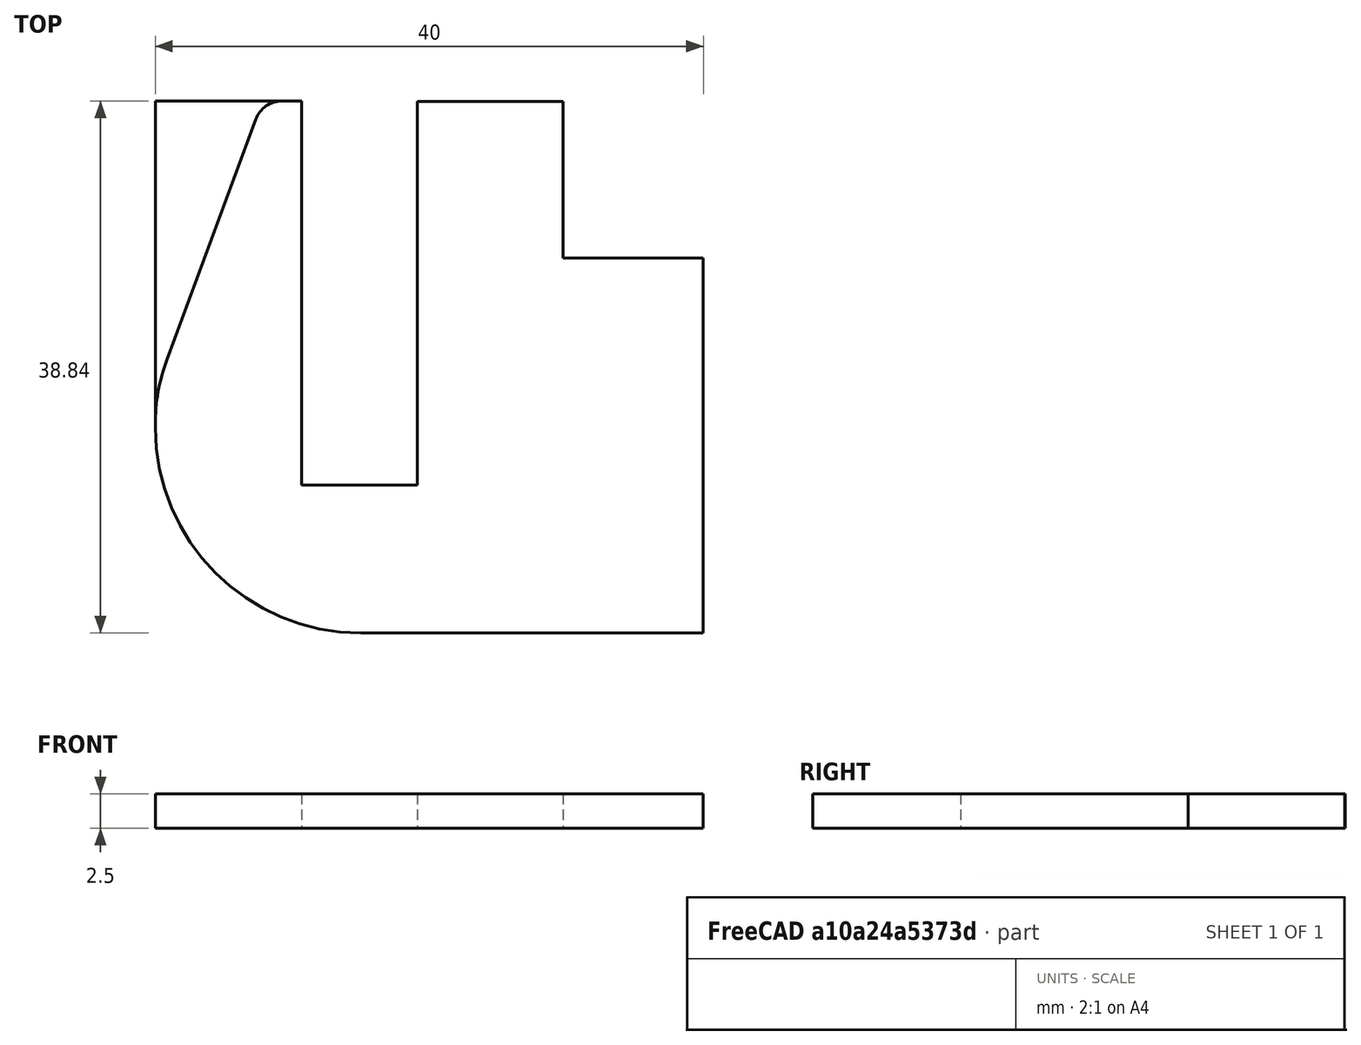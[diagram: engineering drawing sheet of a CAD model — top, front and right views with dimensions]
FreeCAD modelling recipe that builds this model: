
FCSTD DOCUMENT  (FreeCAD 0.16R6703 (Git))
Label: Tampa
License: FreeArt
LicenseURL: http://artlibre.org/licence/lal
objects: PartDesign::Fillet×3, Sketcher::SketchObject×2, Mesh::Feature×1, PartDesign::Pad×1, PartDesign::Pocket×1
note: 9 computed .brp shape members not serialized (recipe doc carries the construction recipe); baked Part::Feature solids carry a one-line shape summary decoded from their .brp

FEATURE [Mesh::Feature] AntiWobble_XIdler_End  label="AntiWobble-XIdler-End"
FEATURE [Sketcher::SketchObject] Sketch
  sketch-geometry (10):
    g0: LineSegment StartX=-14.923 StartY=-19.3714 StartZ=0 EndX=25.077 EndY=-19.3714 EndZ=0
    g1: LineSegment StartX=25.077 StartY=-19.3714 StartZ=0 EndX=25.077 EndY=8 EndZ=0
    g2: LineSegment StartX=25.077 StartY=8 StartZ=0 EndX=14.8408 EndY=8 EndZ=0
    g3: LineSegment StartX=14.8408 StartY=8 StartZ=0 EndX=14.8408 EndY=19.4418 EndZ=0
    g4: LineSegment StartX=14.8408 StartY=19.4418 StartZ=0 EndX=4.2121 EndY=19.4418 EndZ=0
    g5: LineSegment StartX=4.2121 StartY=19.4418 StartZ=0 EndX=4.2121 EndY=-8.58133 EndZ=0
    g6: LineSegment StartX=4.2121 StartY=-8.58133 StartZ=0 EndX=-4.2553 EndY=-8.58133 EndZ=0
    g7: LineSegment StartX=-4.2553 StartY=-8.58133 StartZ=0 EndX=-4.2553 EndY=19.4667 EndZ=0
    g8: LineSegment StartX=-4.2553 StartY=19.4667 StartZ=0 EndX=-14.923 EndY=19.4667 EndZ=0
    g9: LineSegment StartX=-14.923 StartY=19.4667 StartZ=0 EndX=-14.923 EndY=-19.3714 EndZ=0
  constraints (27):
    c: Horizontal(g0)
    c: Coincident(g0,g1)
    c: Vertical(g1)
    c: Coincident(g1,g2)
    c: Horizontal(g2)
    c: Coincident(g2,g3)
    c: Vertical(g3)
    c: Coincident(g3,g4)
    c: Horizontal(g4)
    c: Coincident(g4,g5)
    c: Vertical(g5)
    c: Coincident(g5,g6)
    c: Horizontal(g6)
    c: Coincident(g6,g7)
    c: Vertical(g7)
    c: Coincident(g7,g8)
    c: Horizontal(g8)
    c: Coincident(g8,g9)
    c: Vertical(g9)
    c: Coincident(g0,g9)
    c: Distance(g-1,g0) = 19.3714
    c: Distance(g-1,g9) = 14.923
    c: DistanceX(g0,g0) = 40
    c: DistanceX(g8,g8) = 10.6677
    c: DistanceY(g9,g9) = 38.8381
    c: DistanceX(g4,g4) = 10.6287
    c: DistanceX(g2,g2) = 10.2362
FEATURE [PartDesign::Pad] Pad
  Length = 2.5
  Length2 = 100
  Reversed = true
  Sketch = -> Sketch
  Type = 0
FEATURE [PartDesign::Fillet] Fillet
  Base = -> Pad [Edge1]
  Radius = 15
FEATURE [Sketcher::SketchObject] Sketch001
  Support = -> Fillet [Face2]
  sketch-geometry (3):
    g0: LineSegment StartX=-16.0319 StartY=20.0661 StartZ=0 EndX=-6.85709 EndY=20.0661 EndZ=0
    g1: LineSegment StartX=-6.85709 StartY=20.0661 StartZ=0 EndX=-16.0319 EndY=-4.69657 EndZ=0
    g2: LineSegment StartX=-16.0319 StartY=-4.69657 StartZ=0 EndX=-16.0319 EndY=20.0661 EndZ=0
  constraints (5):
    c: Horizontal(g0)
    c: Coincident(g0,g1)
    c: Coincident(g1,g2)
    c: Coincident(g2,g0)
    c: Vertical(g2)
FEATURE [PartDesign::Pocket] Pocket
  Length = 5
  Sketch = -> Sketch001
  Type = 0
FEATURE [PartDesign::Fillet] Fillet001
  Base = -> Pocket [Edge36]
  Radius = 14
FEATURE [PartDesign::Fillet] Fillet002
  Base = -> Fillet001 [Edge15]
  Radius = 2
